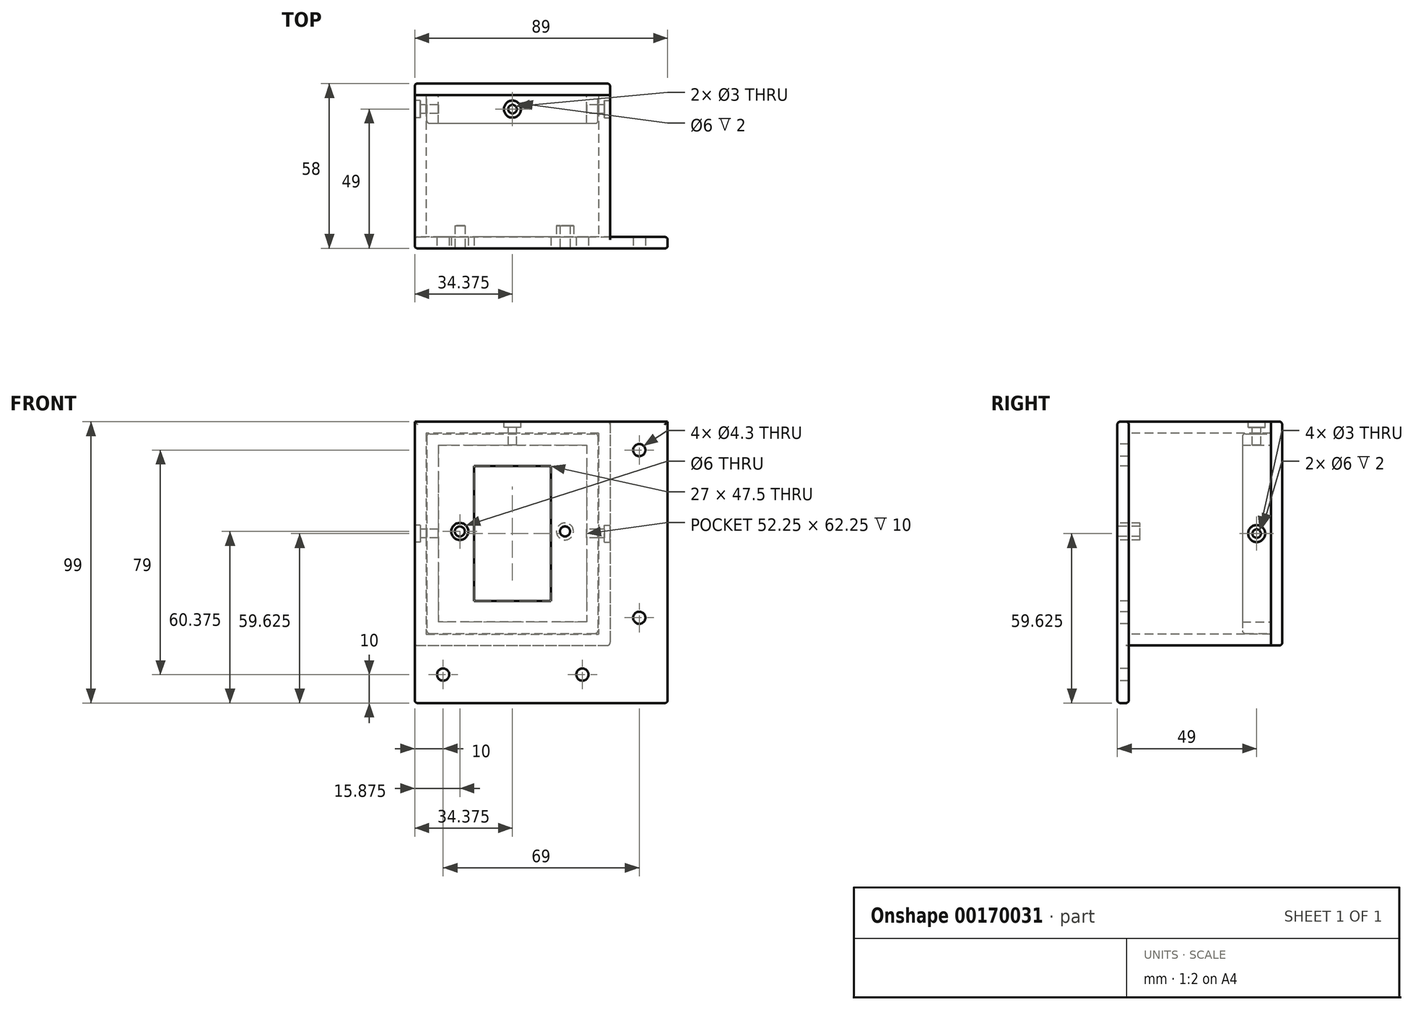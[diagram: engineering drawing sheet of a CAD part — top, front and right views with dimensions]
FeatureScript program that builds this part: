
annotation { "Feature Type Name" : "Feature", "Feature Type Description" : "" }
export const myFeature = defineFeature(function(context is Context, id is Id, definition is map)
    precondition{}
    {
        {
            var Q0;
            Q0=qCreatedBy(makeId("Front.planeOp"),FACE);
            var sketch = newSketch(context, id + "F0", { "sketchPlane" : qUnion([Q0])});
            skLineSegment(sketch, "E0.bottom", {"start": v(0, 0) * mm, "end": v(-89, 0) * mm});
            skLineSegment(sketch, "E0.top", {"start": v(0, 99) * mm, "end": v(-89, 99) * mm});
            skLineSegment(sketch, "E0.left", {"start": v(0, 0) * mm, "end": v(0, 99) * mm});
            skLineSegment(sketch, "E1.0", {"start": v(-41.13, 35.88) * mm, "end": v(-68.13, 35.87) * mm});
            skLineSegment(sketch, "E2.0", {"start": v(-41.13, 35.88) * mm, "end": v(-41.13, 83.38) * mm});
            skLineSegment(sketch, "E3.0", {"start": v(-68.13, 35.87) * mm, "end": v(-68.13, 83.37) * mm});
            skLineSegment(sketch, "E4.0", {"start": v(-41.13, 83.38) * mm, "end": v(-68.13, 83.37) * mm});
            skCircle(sketch, "E5", {"center": v(-36.13, 60.38) * mm, "radius": 1.77 * mm});
            skCircle(sketch, "E6.MirrorC", {"center": v(-73.13, 60.37) * mm, "radius": 1.77 * mm});
            skCircle(sketch, "E7", {"center": v(-73.13, 60.37) * mm, "radius": 3 * mm});
            skCircle(sketch, "E8", {"center": v(-36.13, 60.38) * mm, "radius": 3 * mm});
            skCircle(sketch, "E9", {"center": v(-10, 89) * mm, "radius": 2.15 * mm});
            skCircle(sketch, "E10", {"center": v(-10, 30) * mm, "radius": 2.15 * mm});
            skCircle(sketch, "E11", {"center": v(-79, 10) * mm, "radius": 2.15 * mm});
            skCircle(sketch, "E12", {"center": v(-30, 10) * mm, "radius": 2.15 * mm});
            skLineSegment(sketch, "E13.bottom", {"start": v(-89, 99) * mm, "end": v(-20.25, 99) * mm});
            skLineSegment(sketch, "E14", {"start": v(-89, 99) * mm, "end": v(-89, 0) * mm});
            skSolve(sketch);
        }
        {
            var Q0;
            Q0=makeQuery(id+"F0.imprint","IMPRINT",FACE,{"disambiguationData":[TD([[makeQuery(id+"F0.imprint","IMPRINT",EDGE,{"derivedFrom":sQuery(id+"F0.wireOp",EDGE,"E0.bottom")}),-1.0]])]});
            var Q1;
            Q1=makeQuery(id+"F0.imprint","IMPRINT",FACE,{"disambiguationData":[TD([[makeQuery(id+"F0.imprint","IMPRINT",EDGE,{"derivedFrom":sQuery(id+"F0.wireOp",EDGE,"E6.MirrorC")}),1.0]])]});
            var Q2;
            Q2=makeQuery(id+"F0.imprint","IMPRINT",FACE,{"disambiguationData":[TD([[makeQuery(id+"F0.imprint","IMPRINT",EDGE,{"derivedFrom":sQuery(id+"F0.wireOp",EDGE,"E5")}),-1.0]])]});
            extrude(context, id + "F1", {"entities" : qUnion([Q0, Q1, Q2]), "oppositeDirection" : true, "depth" : 4 * mm});
        }
        {
            var Q0;
            Q0=makeQuery(id+"F0.imprint","IMPRINT",FACE,{"disambiguationData":[TD([[makeQuery(id+"F0.imprint","IMPRINT",EDGE,{"derivedFrom":sQuery(id+"F0.wireOp",EDGE,"E6.MirrorC")}),1.0]])]});
            var Q1;
            Q1=makeQuery(id+"F0.imprint","IMPRINT",FACE,{"disambiguationData":[TD([[makeQuery(id+"F0.imprint","IMPRINT",EDGE,{"derivedFrom":sQuery(id+"F0.wireOp",EDGE,"E5")}),-1.0]])]});
            extrude(context, id + "F2", {"entities" : qUnion([Q0, Q1]), "operationType" : NewBodyOperationType.ADD, "oppositeDirection" : true, "depth" : 8 * mm});
        }
        {
            var Q0;
            Q0=makeQuery(id+"F1.opExtrude","CAP_FACE",FACE,{"disambiguationData":[OSD([sQuery(id+"F0.wireOp",EDGE,"E0.bottom"),sQuery(id+"F0.wireOp",EDGE,"E0.top"),sQuery(id+"F0.wireOp",EDGE,"E0.left"),sQuery(id+"F0.wireOp",EDGE,"E0.right"),sQuery(id+"F0.wireOp",EDGE,"E1.0"),sQuery(id+"F0.wireOp",EDGE,"E2.0"),sQuery(id+"F0.wireOp",EDGE,"E3.0"),sQuery(id+"F0.wireOp",EDGE,"E4.0"),sQuery(id+"F0.wireOp",EDGE,"E5"),sQuery(id+"F0.wireOp",EDGE,"E6.MirrorC"),sQuery(id+"F0.wireOp",EDGE,"E9"),sQuery(id+"F0.wireOp",EDGE,"E10"),sQuery(id+"F0.wireOp",EDGE,"E11"),sQuery(id+"F0.wireOp",EDGE,"E12")])],"isStart":false});
            var sketch = newSketch(context, id + "F3", { "sketchPlane" : qUnion([Q0])});
            skLineSegment(sketch, "E15.left", {"start": v(20.25, 99) * mm, "end": v(20.25, 20.25) * mm});
            skLineSegment(sketch, "E15.right", {"start": v(24.25, 95) * mm, "end": v(24.25, 24.25) * mm});
            skLineSegment(sketch, "E16.bottom", {"start": v(20.25, 99) * mm, "end": v(89, 99) * mm});
            skLineSegment(sketch, "E16.top", {"start": v(24.25, 95) * mm, "end": v(85, 95) * mm});
            skLineSegment(sketch, "E17.left", {"start": v(89, 99) * mm, "end": v(89, 20.25) * mm});
            skLineSegment(sketch, "E17.right", {"start": v(85, 95) * mm, "end": v(85, 24.25) * mm});
            skLineSegment(sketch, "E18.bottom", {"start": v(85, 24.25) * mm, "end": v(24.25, 24.25) * mm});
            skLineSegment(sketch, "E18.top", {"start": v(89, 20.25) * mm, "end": v(20.25, 20.25) * mm});
            skSolve(sketch);
        }
        {
            var Q0;
            Q0=makeQuery(id+"F3.imprint","IMPRINT",FACE,{"disambiguationData":[TD([[makeQuery(id+"F3.imprint","IMPRINT",EDGE,{"derivedFrom":sQuery(id+"F3.wireOp",EDGE,"E15.left")}),1.0]])]});
            extrude(context, id + "F4", {"entities" : qUnion([Q0]), "operationType" : NewBodyOperationType.ADD, "depth" : 50 * mm});
        }
        {
            var Q0;
            Q0=makeQuery(id+"F4.opExtrude","CAP_FACE",FACE,{"disambiguationData":[OSD([sQuery(id+"F3.wireOp",EDGE,"E15.left"),sQuery(id+"F3.wireOp",EDGE,"E15.right"),sQuery(id+"F3.wireOp",EDGE,"E16.bottom"),sQuery(id+"F3.wireOp",EDGE,"E16.top"),sQuery(id+"F3.wireOp",EDGE,"E17.left"),sQuery(id+"F3.wireOp",EDGE,"E17.right"),sQuery(id+"F3.wireOp",EDGE,"E18.bottom"),sQuery(id+"F3.wireOp",EDGE,"E18.top")])],"isStart":false});
            var sketch = newSketch(context, id + "F5", { "sketchPlane" : qUnion([Q0])});
            skLineSegment(sketch, "E19.bottom", {"start": v(20.25, 99) * mm, "end": v(89, 99) * mm});
            skLineSegment(sketch, "E19.top", {"start": v(20.25, 20.25) * mm, "end": v(89, 20.25) * mm});
            skLineSegment(sketch, "E19.left", {"start": v(20.25, 99) * mm, "end": v(20.25, 20.25) * mm});
            skLineSegment(sketch, "E19.right", {"start": v(89, 99) * mm, "end": v(89, 20.25) * mm});
            skSolve(sketch);
        }
        {
            var Q0;
            Q0 = qSketchRegion(id + "F5", true);
            extrude(context, id + "F6", {"entities" : qUnion([Q0]), "depth" : 4 * mm});
        }
        {
            var Q0;
            Q0=makeQuery(id+"F6.opExtrude","CAP_FACE",FACE,{"disambiguationData":[OSD([sQuery(id+"F5.wireOp",EDGE,"E19.bottom"),sQuery(id+"F5.wireOp",EDGE,"E19.top"),sQuery(id+"F5.wireOp",EDGE,"E19.left"),sQuery(id+"F5.wireOp",EDGE,"E19.right")])],"isStart":true});
            var sketch = newSketch(context, id + "F7", { "sketchPlane" : qUnion([Q0])});
            skLineSegment(sketch, "E20.bottom", {"start": v(-84.75, 94.75) * mm, "end": v(-80.75, 94.75) * mm});
            skLineSegment(sketch, "E20.top", {"start": v(-84.75, 24.5) * mm, "end": v(-80.75, 24.5) * mm});
            skLineSegment(sketch, "E20.left", {"start": v(-84.75, 94.75) * mm, "end": v(-84.75, 24.5) * mm});
            skLineSegment(sketch, "E20.right", {"start": v(-80.75, 90.75) * mm, "end": v(-80.75, 28.5) * mm});
            skLineSegment(sketch, "E21.MirrorCS", {"start": v(-24.5, 24.5) * mm, "end": v(-28.5, 24.5) * mm});
            skLineSegment(sketch, "E22.MirrorCS", {"start": v(-24.5, 94.75) * mm, "end": v(-28.5, 94.75) * mm});
            skLineSegment(sketch, "E23.MirrorCS", {"start": v(-24.5, 94.75) * mm, "end": v(-24.5, 24.5) * mm});
            skLineSegment(sketch, "E24.MirrorCS", {"start": v(-28.5, 90.75) * mm, "end": v(-28.5, 28.5) * mm});
            skLineSegment(sketch, "E25.bottom", {"start": v(-80.75, 94.75) * mm, "end": v(-28.5, 94.75) * mm});
            skLineSegment(sketch, "E25.top", {"start": v(-80.75, 90.75) * mm, "end": v(-28.5, 90.75) * mm});
            skLineSegment(sketch, "E26.bottom", {"start": v(-28.5, 24.5) * mm, "end": v(-80.75, 24.5) * mm});
            skLineSegment(sketch, "E26.top", {"start": v(-28.5, 28.5) * mm, "end": v(-80.75, 28.5) * mm});
            skSolve(sketch);
        }
        {
            var Q0;
            Q0=makeQuery(id+"F7.imprint","IMPRINT",FACE,{"disambiguationData":[TD([[makeQuery(id+"F7.imprint","IMPRINT",EDGE,{"derivedFrom":sQuery(id+"F7.wireOp",EDGE,"E20.bottom")}),-1.0]])]});
            extrude(context, id + "F8", {"entities" : qUnion([Q0]), "operationType" : NewBodyOperationType.ADD, "depth" : 10 * mm});
        }
        {
            var Q0;
            Q0=makeQuery(id+"F8.opExtrude","CAP_EDGE",EDGE,{"disambiguationData":[OSD([sQuery(id+"F7.wireOp",EDGE,"E20.bottom"),sQuery(id+"F7.wireOp",EDGE,"E22.MirrorCS"),sQuery(id+"F7.wireOp",EDGE,"E25.bottom")])],"isStart":false});
            var Q1;
            Q1=makeQuery(id+"F8.opExtrude","CAP_EDGE",EDGE,{"disambiguationData":[OSD([sQuery(id+"F7.wireOp",EDGE,"E20.left")])],"isStart":false});
            var Q2;
            Q2=makeQuery(id+"F8.opExtrude","CAP_EDGE",EDGE,{"disambiguationData":[OSD([sQuery(id+"F7.wireOp",EDGE,"E23.MirrorCS")])],"isStart":false});
            var Q3;
            Q3=makeQuery(id+"F8.opExtrude","CAP_EDGE",EDGE,{"disambiguationData":[OSD([sQuery(id+"F7.wireOp",EDGE,"E20.top"),sQuery(id+"F7.wireOp",EDGE,"E21.MirrorCS"),sQuery(id+"F7.wireOp",EDGE,"E26.bottom")])],"isStart":false});
            var Q4;
            Q4=makeQuery(id+"F8.opExtrude","SWEPT_EDGE",EDGE,{"disambiguationData":[OSD([sQuery(id+"F7.wireOp",EDGE,"E20.bottom"),sQuery(id+"F7.wireOp",EDGE,"E20.left")])]});
            var Q5;
            Q5=makeQuery(id+"F8.opExtrude","SWEPT_EDGE",EDGE,{"disambiguationData":[OSD([sQuery(id+"F7.wireOp",EDGE,"E20.top"),sQuery(id+"F7.wireOp",EDGE,"E20.left")])]});
            var Q6;
            Q6=makeQuery(id+"F8.opExtrude","SWEPT_EDGE",EDGE,{"disambiguationData":[OSD([sQuery(id+"F7.wireOp",EDGE,"E21.MirrorCS"),sQuery(id+"F7.wireOp",EDGE,"E23.MirrorCS")])]});
            var Q7;
            Q7=makeQuery(id+"F8.opExtrude","SWEPT_EDGE",EDGE,{"disambiguationData":[OSD([sQuery(id+"F7.wireOp",EDGE,"E22.MirrorCS"),sQuery(id+"F7.wireOp",EDGE,"E23.MirrorCS")])]});
            fillet(context, id + "F9", {"entities" : qUnion([Q0, Q1, Q2, Q3, Q4, Q5, Q6, Q7]), "radius" : 1 * mm, "tangentPropagation" : true, "allowEdgeOverflow" : false});
        }
        {
            var Q0;
            Q0=makeQuery(id+"F4.boolean.opBoolean","MERGE",FACE,{"derivedFrom":[makeQuery(id+"F1.opExtrude","SWEPT_FACE",FACE,{"disambiguationData":[OSD([sQuery(id+"F0.wireOp",EDGE,"E0.top"),sQuery(id+"F0.wireOp",EDGE,"E13.bottom")])]}),makeQuery(id+"F4.opExtrude","SWEPT_FACE",FACE,{"disambiguationData":[OSD([sQuery(id+"F3.wireOp",EDGE,"E16.bottom")])]})]});
            var sketch = newSketch(context, id + "F10", { "sketchPlane" : qUnion([Q0])});
            skCircle(sketch, "E27", {"center": v(-54.62, 49) * mm, "radius": 1.5 * mm});
            skPoint(sketch, "E27.centerSnap0", {"position": v(-54.62, 54) * mm});
            skCircle(sketch, "E28", {"center": v(-54.62, 49) * mm, "radius": 3 * mm});
            skSolve(sketch);
        }
        {
            var Q0;
            Q0=makeQuery(id+"F10.imprint","IMPRINT",FACE,{"disambiguationData":[TD([[makeQuery(id+"F10.imprint","IMPRINT",EDGE,{"derivedFrom":sQuery(id+"F10.wireOp",EDGE,"E27")}),1.0]])]});
            extrude(context, id + "F11", {"entities" : qUnion([Q0]), "operationType" : NewBodyOperationType.REMOVE, "oppositeDirection" : true, "depth" : 25 * mm});
        }
        {
            var Q0;
            Q0=makeQuery(id+"F10.imprint","IMPRINT",FACE,{"disambiguationData":[TD([[makeQuery(id+"F10.imprint","IMPRINT",EDGE,{"derivedFrom":sQuery(id+"F10.wireOp",EDGE,"E27")}),-1.0]])]});
            extrude(context, id + "F12", {"entities" : qUnion([Q0]), "operationType" : NewBodyOperationType.REMOVE, "oppositeDirection" : true, "depth" : 2 * mm});
        }
        {
            var Q0;
            Q0=makeQuery(id+"F4.boolean.opBoolean","MERGE",FACE,{"derivedFrom":[makeQuery(id+"F1.opExtrude","SWEPT_FACE",FACE,{"disambiguationData":[OSD([sQuery(id+"F0.wireOp",EDGE,"E14")])]}),makeQuery(id+"F4.opExtrude","SWEPT_FACE",FACE,{"disambiguationData":[OSD([sQuery(id+"F3.wireOp",EDGE,"E17.left")])]})]});
            var sketch = newSketch(context, id + "F13", { "sketchPlane" : qUnion([Q0])});
            skCircle(sketch, "E29", {"center": v(-49, 59.63) * mm, "radius": 1.5 * mm});
            skPoint(sketch, "E29.centerSnap0", {"position": v(-54, 59.63) * mm});
            skCircle(sketch, "E30", {"center": v(-49, 59.63) * mm, "radius": 3 * mm});
            skSolve(sketch);
        }
        {
            var Q0;
            Q0=makeQuery(id+"F13.imprint","IMPRINT",FACE,{"disambiguationData":[TD([[makeQuery(id+"F13.imprint","IMPRINT",EDGE,{"derivedFrom":sQuery(id+"F13.wireOp",EDGE,"E29")}),1.0]])]});
            extrude(context, id + "F14", {"entities" : qUnion([Q0]), "operationType" : NewBodyOperationType.REMOVE, "endBound" : BoundingType.THROUGH_ALL, "oppositeDirection" : true, "depth" : 50 * mm});
        }
        {
            var Q0;
            Q0=makeQuery(id+"F13.imprint","IMPRINT",FACE,{"disambiguationData":[TD([[makeQuery(id+"F13.imprint","IMPRINT",EDGE,{"derivedFrom":sQuery(id+"F13.wireOp",EDGE,"E29")}),-1.0]])]});
            extrude(context, id + "F15", {"entities" : qUnion([Q0]), "operationType" : NewBodyOperationType.REMOVE, "oppositeDirection" : true, "depth" : 2 * mm});
        }
        {
            var Q0;
            Q0=makeQuery(id+"F4.opExtrude","SWEPT_FACE",FACE,{"disambiguationData":[OSD([sQuery(id+"F3.wireOp",EDGE,"E15.left")])]});
            var sketch = newSketch(context, id + "F16", { "sketchPlane" : qUnion([Q0])});
            skCircle(sketch, "E31", {"center": v(49, 59.63) * mm, "radius": 3 * mm});
            skSolve(sketch);
        }
        {
            var Q0;
            Q0=makeQuery(id+"F16.imprint","IMPRINT",FACE,{"disambiguationData":[TD([[makeQuery(id+"F16.imprint","IMPRINT",EDGE,{"derivedFrom":sQuery(id+"F16.wireOp",EDGE,"E31")}),1.0]])]});
            extrude(context, id + "F17", {"entities" : qUnion([Q0]), "operationType" : NewBodyOperationType.REMOVE, "oppositeDirection" : true, "depth" : 2 * mm});
        }
        {
            var Q0;
            Q0=makeQuery(id+"F1.opExtrude","SWEPT_EDGE",EDGE,{"disambiguationData":[OSD([sQuery(id+"F0.wireOp",EDGE,"E0.bottom"),sQuery(id+"F0.wireOp",EDGE,"E0.left")])]});
            var Q1;
            Q1=makeQuery(id+"F1.opExtrude","CAP_EDGE",EDGE,{"disambiguationData":[OSD([sQuery(id+"F0.wireOp",EDGE,"E0.left")])],"isStart":true});
            var Q2;
            Q2=makeQuery(id+"F1.opExtrude","CAP_EDGE",EDGE,{"disambiguationData":[OSD([sQuery(id+"F0.wireOp",EDGE,"E0.bottom")])],"isStart":true});
            var Q3;
            Q3=makeQuery(id+"F1.opExtrude","CAP_EDGE",EDGE,{"disambiguationData":[OSD([sQuery(id+"F0.wireOp",EDGE,"E14")])],"isStart":true});
            var Q4;
            Q4=makeQuery(id+"F1.opExtrude","CAP_EDGE",EDGE,{"disambiguationData":[OSD([sQuery(id+"F0.wireOp",EDGE,"E0.top"),sQuery(id+"F0.wireOp",EDGE,"E13.bottom")])],"isStart":true});
            var Q5;
            Q5=makeQuery(id+"F1.opExtrude","SWEPT_EDGE",EDGE,{"disambiguationData":[OSD([sQuery(id+"F0.wireOp",EDGE,"E0.bottom"),sQuery(id+"F0.wireOp",EDGE,"E14")])]});
            var Q6;
            Q6=makeQuery(id+"F1.opExtrude","CAP_EDGE",EDGE,{"disambiguationData":[OSD([sQuery(id+"F0.wireOp",EDGE,"E14")])],"isStart":false});
            var Q7;
            Q7=makeQuery(id+"F4.boolean.opBoolean","MERGE",EDGE,{"derivedFrom":[makeQuery(id+"F1.opExtrude","SWEPT_EDGE",EDGE,{"disambiguationData":[OSD([sQuery(id+"F0.wireOp",EDGE,"E13.bottom"),sQuery(id+"F0.wireOp",EDGE,"E14")])]}),makeQuery(id+"F4.opExtrude","SWEPT_EDGE",EDGE,{"disambiguationData":[OSD([sQuery(id+"F3.wireOp",EDGE,"E16.bottom"),sQuery(id+"F3.wireOp",EDGE,"E17.left")])]})]});
            var Q8;
            Q8=makeQuery(id+"F4.opExtrude","CAP_EDGE",EDGE,{"disambiguationData":[OSD([sQuery(id+"F3.wireOp",EDGE,"E15.left")])],"isStart":true});
            var Q9;
            Q9=makeQuery(id+"F4.opExtrude","SWEPT_EDGE",EDGE,{"disambiguationData":[OSD([sQuery(id+"F3.wireOp",EDGE,"E15.left"),sQuery(id+"F3.wireOp",EDGE,"E18.top")])]});
            var Q10;
            Q10=makeQuery(id+"F1.opExtrude","CAP_EDGE",EDGE,{"disambiguationData":[OSD([sQuery(id+"F0.wireOp",EDGE,"E0.bottom")])],"isStart":false});
            var Q11;
            Q11=makeQuery(id+"F1.opExtrude","CAP_EDGE",EDGE,{"disambiguationData":[OSD([sQuery(id+"F0.wireOp",EDGE,"E0.left")])],"isStart":false});
            var Q12;
            Q12=makeQuery(id+"F1.opExtrude","CAP_EDGE",EDGE,{"disambiguationData":[OSD([sQuery(id+"F0.wireOp",EDGE,"E0.top"),sQuery(id+"F0.wireOp",EDGE,"E13.bottom")])],"isStart":false});
            var Q13;
            Q13=makeQuery(id+"F6.opExtrude","CAP_EDGE",EDGE,{"disambiguationData":[OSD([sQuery(id+"F5.wireOp",EDGE,"E19.bottom")])],"isStart":false});
            var Q14;
            Q14=makeQuery(id+"F6.opExtrude","SWEPT_EDGE",EDGE,{"disambiguationData":[OSD([sQuery(id+"F5.wireOp",EDGE,"E19.bottom"),sQuery(id+"F5.wireOp",EDGE,"E19.left")])]});
            var Q15;
            Q15=makeQuery(id+"F6.opExtrude","CAP_EDGE",EDGE,{"disambiguationData":[OSD([sQuery(id+"F5.wireOp",EDGE,"E19.left")])],"isStart":false});
            var Q16;
            Q16=makeQuery(id+"F6.opExtrude","SWEPT_EDGE",EDGE,{"disambiguationData":[OSD([sQuery(id+"F5.wireOp",EDGE,"E19.top"),sQuery(id+"F5.wireOp",EDGE,"E19.left")])]});
            var Q17;
            Q17=makeQuery(id+"F6.opExtrude","CAP_EDGE",EDGE,{"disambiguationData":[OSD([sQuery(id+"F5.wireOp",EDGE,"E19.top")])],"isStart":false});
            var Q18;
            Q18=makeQuery(id+"F6.opExtrude","SWEPT_EDGE",EDGE,{"disambiguationData":[OSD([sQuery(id+"F5.wireOp",EDGE,"E19.top"),sQuery(id+"F5.wireOp",EDGE,"E19.right")])]});
            var Q19;
            Q19=makeQuery(id+"F6.opExtrude","CAP_EDGE",EDGE,{"disambiguationData":[OSD([sQuery(id+"F5.wireOp",EDGE,"E19.right")])],"isStart":false});
            fillet(context, id + "F18", {"entities" : qUnion([Q0, Q1, Q2, Q3, Q4, Q5, Q6, Q7, Q8, Q9, Q10, Q11, Q12, Q13, Q14, Q15, Q16, Q17, Q18, Q19]), "radius" : 1 * mm, "tangentPropagation" : true, "allowEdgeOverflow" : false});
        }
    });
